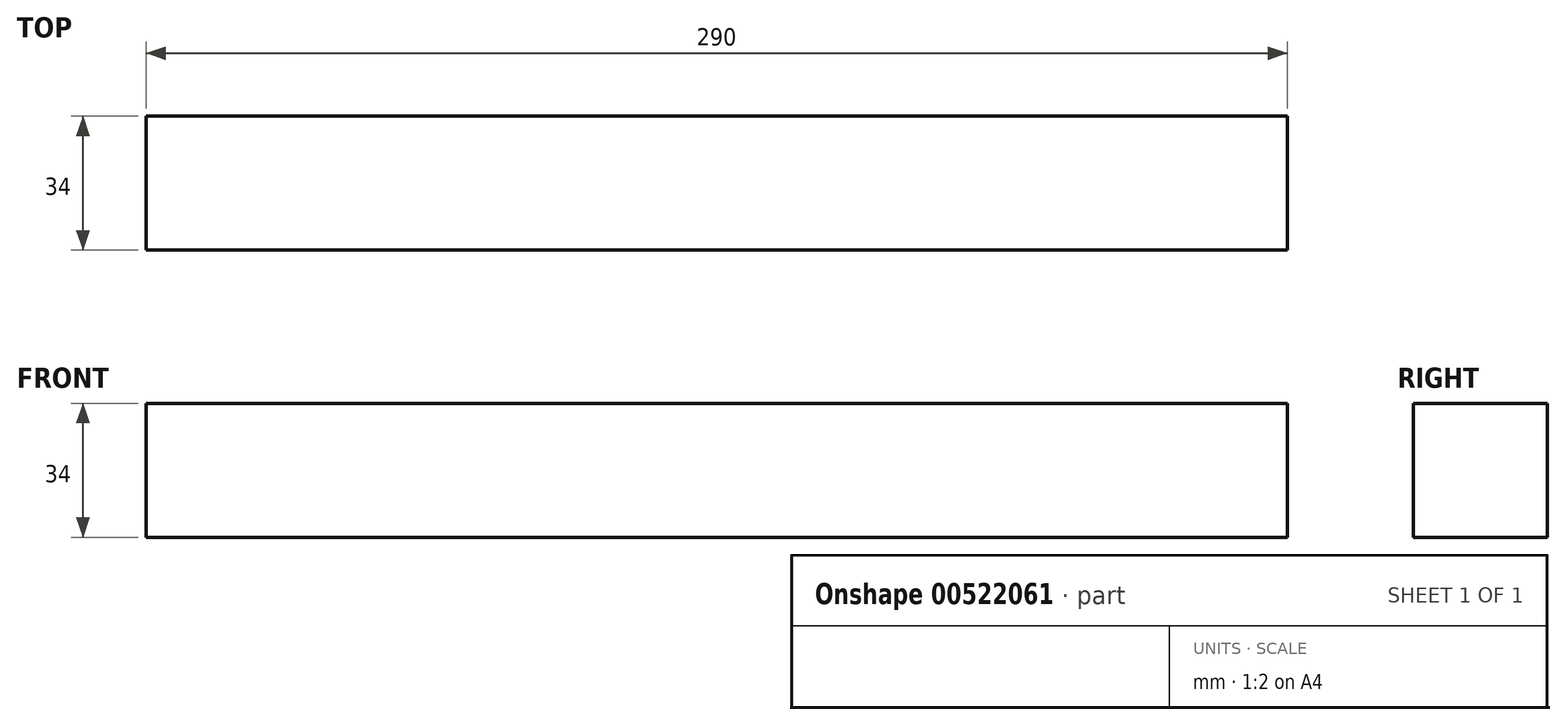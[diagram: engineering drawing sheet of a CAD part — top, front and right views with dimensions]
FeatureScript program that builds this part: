
annotation { "Feature Type Name" : "Feature", "Feature Type Description" : "" }
export const myFeature = defineFeature(function(context is Context, id is Id, definition is map)
    precondition{}
    {
        {
            var Q0;
            Q0=qCreatedBy(makeId("Right.planeOp"),FACE);
            var sketch = newSketch(context, id + "F0", { "sketchPlane" : qUnion([Q0])});
            skLineSegment(sketch, "E0.bottom", {"start": v(0, 0) * mm, "end": v(-34, 0) * mm});
            skLineSegment(sketch, "E0.top", {"start": v(0, 34) * mm, "end": v(-34, 34) * mm});
            skLineSegment(sketch, "E0.left", {"start": v(0, 0) * mm, "end": v(0, 34) * mm});
            skLineSegment(sketch, "E0.right", {"start": v(-34, 0) * mm, "end": v(-34, 34) * mm});
            skSolve(sketch);
        }
        {
            var Q0;
            Q0=makeQuery(id+"F0.imprint","IMPRINT",FACE,{"disambiguationData":[TD([[makeQuery(id+"F0.imprint","IMPRINT",EDGE,{"derivedFrom":sQuery(id+"F0.wireOp",EDGE,"E0.bottom")}),-1.0]])]});
            extrude(context, id + "F1", {"entities" : qUnion([Q0]), "oppositeDirection" : true, "depth" : (356 - 100 + 34) * mm, "offsetDistance" : 25 * mm});
        }
    });
